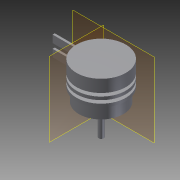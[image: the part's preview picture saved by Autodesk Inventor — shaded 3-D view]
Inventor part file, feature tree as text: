
AUTODESK INVENTOR PART (.ipt)
format: ipt  version: 2012 (Build 160160000, 160)  size: 169,472 bytes
history: native  units: in
note: dims shown in document units (in); Inventor stores cm internally (conversion verified against a paired STEP export)
features: sketch x3, plane x2, extrude x2, revolve x1, reference x1
ambient origin geometry x8: Origin, YZ Plane, XZ Plane, XY Plane, X Axis, Y Axis, Z Axis, Center Point
bodies: Solid1 (feature_tree)
feature tree (9):
  revolve  "Revolution1"  [1 undecoded]
  plane  "Work Plane4"
  extrude  "Extrusion2"  Depth=0.3937in
  plane  "Work Plane5"
  extrude  "Extrusion3"  Depth=0.3937in
  sketch  "Sketch1"  dims[d0=0.0984in d1=0.7874in]
  sketch  "Sketch6"  dims[d3=0.1969in d4=0.3937in]
  reference  "Reference1"
  sketch  "Sketch7"  dims[d7=90.0deg d22=0.3937in d24=1.1811in d26=0.0787in d27=0.9843in d28=0.3937in d29=1.1811in d30=0.7087in d35=0.8312in d36=0.7906in d37=0.0in d38=0.0in d39=0.2362in d40=0.2362in d41=0.3937in d42=0.0703in d43=0.0703in d44=0.4085in d45=0.025in d46=0.025in d47=0.3428in d48=0.1969in d49=0.1969in d50=1.4355in d51=0.1553in d52=0.0in d53=0.0in]
note: 1 required parameter value undecoded (feature->parameter linkage not recoverable at this tier; creation-order binding heuristic only, values carry confidence <= 0.55)
